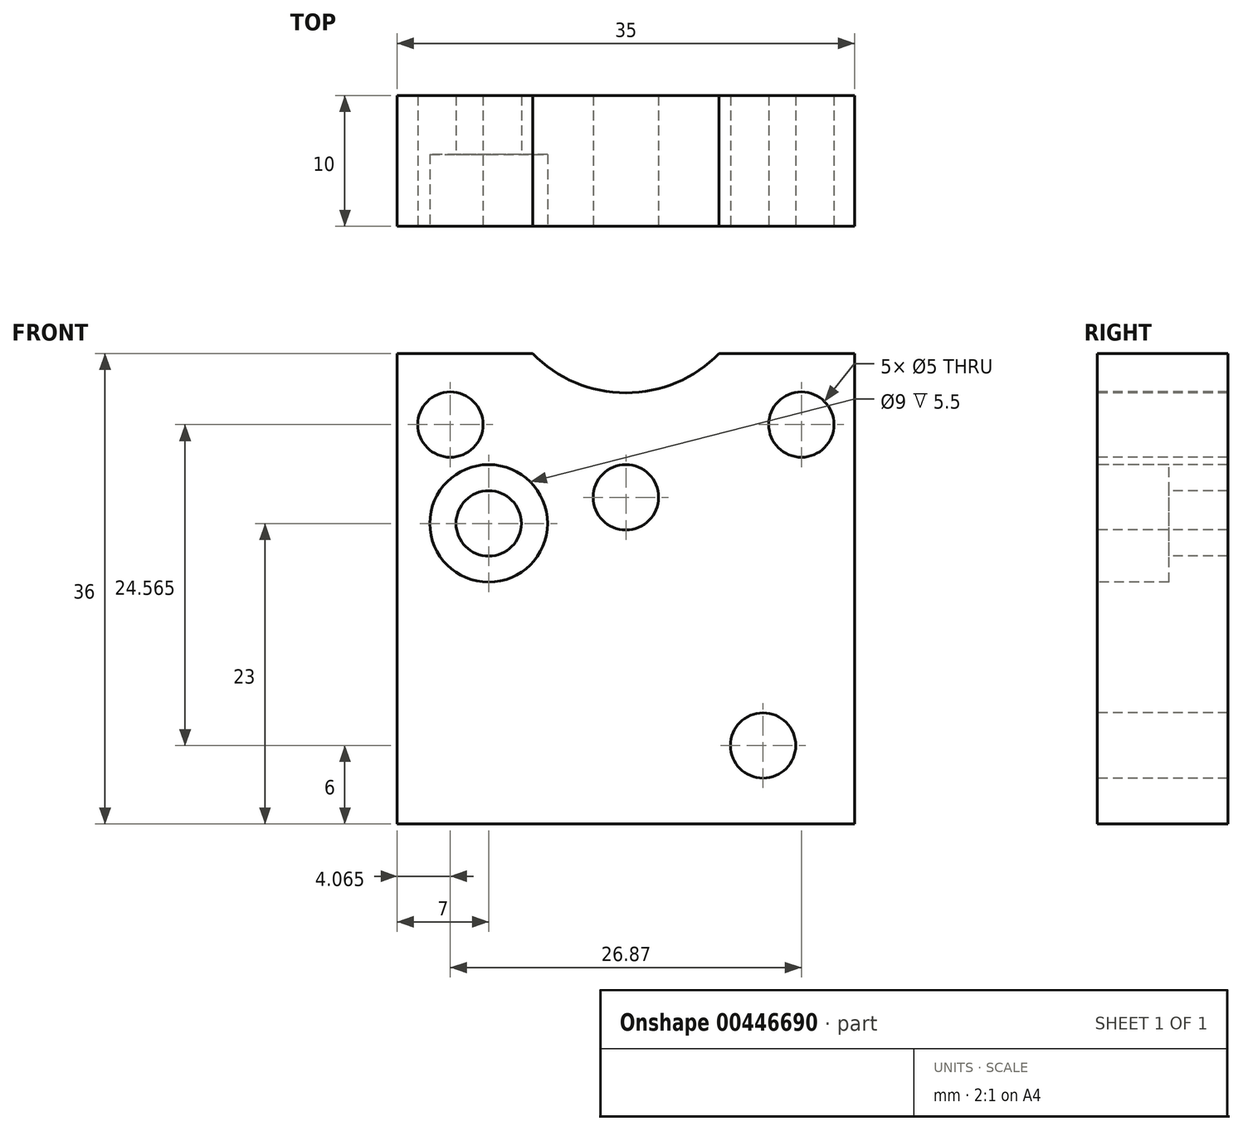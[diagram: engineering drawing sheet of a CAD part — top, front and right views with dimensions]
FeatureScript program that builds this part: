
annotation { "Feature Type Name" : "Feature", "Feature Type Description" : "" }
export const myFeature = defineFeature(function(context is Context, id is Id, definition is map)
    precondition{}
    {
        {
            var Q0;
            Q0=qCreatedBy(makeId("Front.planeOp"),FACE);
            var sketch = newSketch(context, id + "F0", { "sketchPlane" : qUnion([Q0])});
            skLineSegment(sketch, "E0.bottom", {"start": v(0, 0) * mm, "end": v(35, 0) * mm});
            skLineSegment(sketch, "E0.top", {"start": v(0, 50) * mm, "end": v(35, 50) * mm});
            skLineSegment(sketch, "E0.left", {"start": v(0, 0) * mm, "end": v(0, 50) * mm});
            skLineSegment(sketch, "E0.right", {"start": v(35, 0) * mm, "end": v(35, 50) * mm});
            skSolve(sketch);
        }
        {
            var Q0;
            Q0=makeQuery(id+"F0.imprint","IMPRINT",FACE,{"disambiguationData":[TD([[makeQuery(id+"F0.imprint","IMPRINT",EDGE,{"derivedFrom":sQuery(id+"F0.wireOp",EDGE,"E0.bottom")}),1.0]])]});
            extrude(context, id + "F1", {"entities" : qUnion([Q0]), "oppositeDirection" : true, "depth" : 10 * mm});
        }
        {
            var Q0;
            Q0=makeQuery(id+"F1.opExtrude","CAP_FACE",FACE,{"disambiguationData":[OSD([sQuery(id+"F0.wireOp",EDGE,"E0.bottom"),sQuery(id+"F0.wireOp",EDGE,"E0.top"),sQuery(id+"F0.wireOp",EDGE,"E0.left"),sQuery(id+"F0.wireOp",EDGE,"E0.right")])],"isStart":true});
            var sketch = newSketch(context, id + "F2", { "sketchPlane" : qUnion([Q0])});
            skCircle(sketch, "E1", {"center": v(28, 6) * mm, "radius": 2.5 * mm});
            skCircle(sketch, "E2", {"center": v(7, 23) * mm, "radius": 2.5 * mm});
            skSolve(sketch);
        }
        {
            var Q0;
            Q0 = qSketchRegion(id + "F2", true);
            extrude(context, id + "F3", {"entities" : qUnion([Q0]), "operationType" : NewBodyOperationType.REMOVE, "endBound" : BoundingType.THROUGH_ALL, "oppositeDirection" : true, "depth" : 25 * mm});
        }
        {
            var Q0;
            Q0=makeQuery(id+"F1.opExtrude","CAP_FACE",FACE,{"disambiguationData":[OSD([sQuery(id+"F0.wireOp",EDGE,"E0.bottom"),sQuery(id+"F0.wireOp",EDGE,"E0.top"),sQuery(id+"F0.wireOp",EDGE,"E0.left"),sQuery(id+"F0.wireOp",EDGE,"E0.right")])],"isStart":true});
            var sketch = newSketch(context, id + "F4", { "sketchPlane" : qUnion([Q0])});
            skPoint(sketch, "E3", {"position": v(17.5, 44) * mm});
            skPoint(sketch, "E3.positionSnap0", {"position": v(17.5, 0) * mm});
            skCircle(sketch, "E4", {"center": v(17.5, 25) * mm, "radius": 2.5 * mm});
            skCircle(sketch, "E5.2.0", {"center": v(4.06, 30.56) * mm, "radius": 2.5 * mm});
            skLineSegment(sketch, "E5.anchor1", {"start": v(17.5, 44) * mm, "end": v(17.5, 25) * mm, "construction": true});
            skLineSegment(sketch, "E5.anchor2", {"start": v(17.5, 44) * mm, "end": v(4.06, 30.56) * mm, "construction": true});
            skLineSegment(sketch, "E6", {"start": v(17.5, 0) * mm, "end": v(17.5, 50) * mm, "construction": true});
            skCircle(sketch, "E7.MirrorC", {"center": v(30.94, 30.56) * mm, "radius": 2.5 * mm});
            skSolve(sketch);
        }
        {
            var Q0;
            Q0 = qSketchRegion(id + "F4", true);
            extrude(context, id + "F5", {"entities" : qUnion([Q0]), "operationType" : NewBodyOperationType.REMOVE, "oppositeDirection" : true, "depth" : 25 * mm});
        }
        {
            var Q0;
            Q0=makeQuery(id+"F1.opExtrude","CAP_FACE",FACE,{"disambiguationData":[OSD([sQuery(id+"F0.wireOp",EDGE,"E0.bottom"),sQuery(id+"F0.wireOp",EDGE,"E0.top"),sQuery(id+"F0.wireOp",EDGE,"E0.left"),sQuery(id+"F0.wireOp",EDGE,"E0.right")])],"isStart":true});
            var sketch = newSketch(context, id + "F6", { "sketchPlane" : qUnion([Q0])});
            skArc(sketch, "E8", {"start": v(10.36, 36) * mm, "mid": v(17.5, 33) * mm, "end": v(24.64, 36) * mm});
            skPoint(sketch, "E8.centerSnap0", {"position": v(17.5, 0) * mm});
            skLineSegment(sketch, "E9", {"start": v(0, 36) * mm, "end": v(10.36, 36) * mm});
            skLineSegment(sketch, "E10.trimOffspring", {"start": v(24.64, 36) * mm, "end": v(35, 36) * mm});
            skLineSegment(sketch, "E11", {"start": v(0, 36) * mm, "end": v(0, 50) * mm});
            skLineSegment(sketch, "E12", {"start": v(0, 50) * mm, "end": v(35, 50) * mm});
            skLineSegment(sketch, "E13", {"start": v(35, 50) * mm, "end": v(35, 36) * mm});
            skSolve(sketch);
        }
        {
            var Q0;
            Q0 = qSketchRegion(id + "F6", true);
            extrude(context, id + "F7", {"entities" : qUnion([Q0]), "operationType" : NewBodyOperationType.REMOVE, "oppositeDirection" : true, "depth" : 25 * mm});
        }
        {
            var Q0;
            Q0=makeQuery(id+"F1.opExtrude","CAP_FACE",FACE,{"disambiguationData":[OSD([sQuery(id+"F0.wireOp",EDGE,"E0.bottom"),sQuery(id+"F0.wireOp",EDGE,"E0.top"),sQuery(id+"F0.wireOp",EDGE,"E0.left"),sQuery(id+"F0.wireOp",EDGE,"E0.right")])],"isStart":true});
            var sketch = newSketch(context, id + "F8", { "sketchPlane" : qUnion([Q0])});
            skCircle(sketch, "E14", {"center": v(7, 23) * mm, "radius": 4.5 * mm});
            skSolve(sketch);
        }
        {
            var Q0;
            Q0 = qSketchRegion(id + "F8", true);
            extrude(context, id + "F9", {"entities" : qUnion([Q0]), "operationType" : NewBodyOperationType.REMOVE, "oppositeDirection" : true, "depth" : 5.5 * mm});
        }
    });
